# Revit family: Fitting-Flat_Plate-Unistrut-P2862
name_source: partatom
category: Specialty Equipment
revit_build: Autodesk Revit MEP 2012 (Build: 20110309_2315(x64)
units: mm (PartAtom-declared; Revit-internal decimal feet)

## types (3) — shared parameters
04 CSI = 26 05 48
95 CSI = 16070
Assembly Code = D5020100
Bolt Size = 0' - 0 5/16"
CAD URL = http://unistrut.us
Literature URL = http://unistrut.us
Load Capacity Note = Visit the product page for load application and capacity.
Manufacturer = Unistrut by Atkore International
Manufacturer Fax = 708-339-7814
Model = P2862
Overall Length = 0' - 1 5/8"
Overall Width = 0' - 1 5/8"
Part Type = Fitting
Power Strut Part Number = PS 2504
Product Page URL = http://unistrut.us
Subcategory = Flat Plate Fittings
Thickness = 0' - 0 1/4"
URL = http://unistrut.us
Unistrut Part Number = P2862
Unit = <By Category>
ecoScorecard Product Page = http://products.ecoscorecard.com
ecoScorecard_data = http://products.ecoscorecard.com

## per-type parameters (varying)
| type | Hole Diameter | Weight Per Piece |
| P2862 | 0' - 0 11/32" | 0.18 lb |
| P2863 | 0' - 0 7/16" | 0.18 lb |
| P2864 | 0' - 0 9/16" | 0.17 lb |

## geometry (parser evidence)
native form markers: Sweep x4
no freeform markers — native parametric forms only
